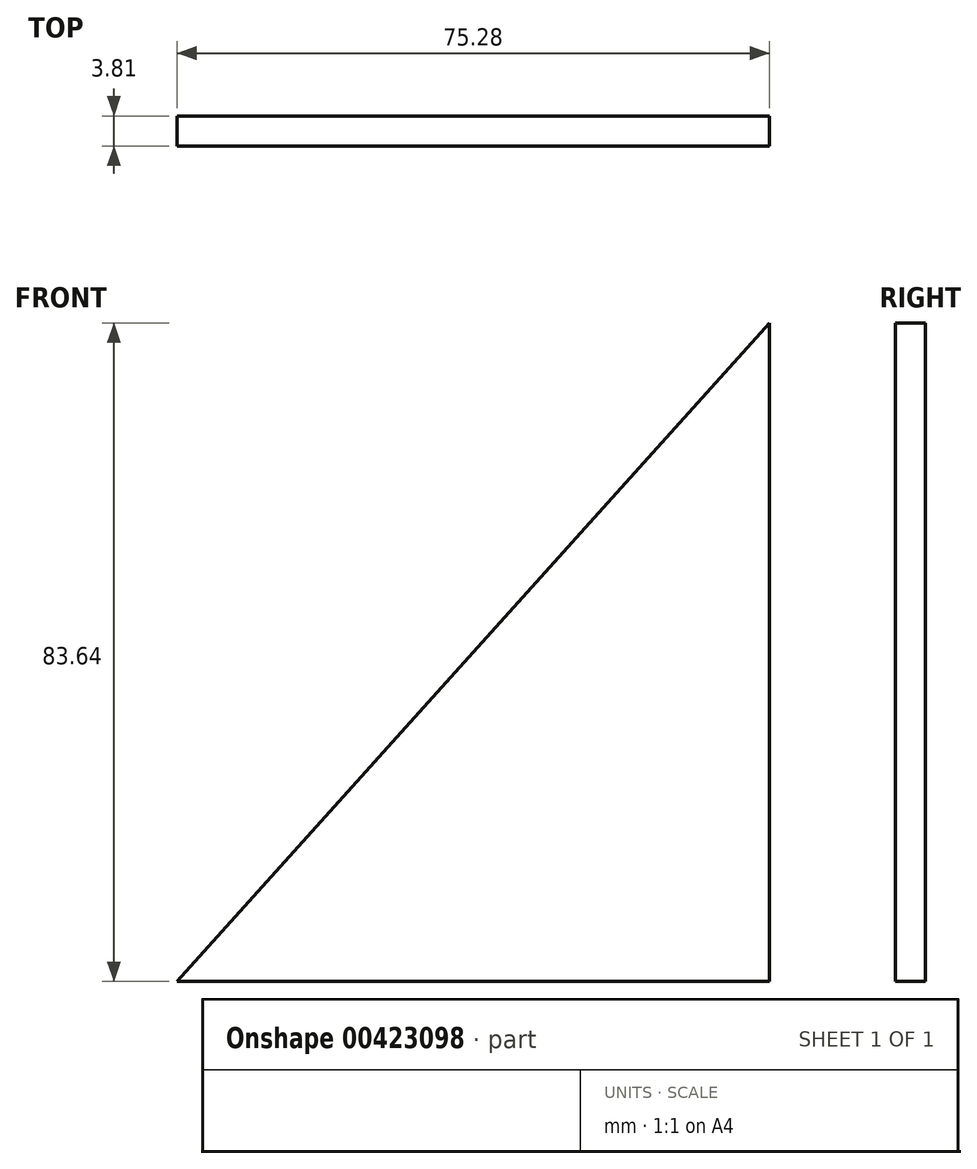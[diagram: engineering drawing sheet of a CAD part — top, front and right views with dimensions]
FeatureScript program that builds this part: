
annotation { "Feature Type Name" : "Feature", "Feature Type Description" : "" }
export const myFeature = defineFeature(function(context is Context, id is Id, definition is map)
    precondition{}
    {
        {
            var Q0;
            Q0=qCreatedBy(makeId("Front.planeOp"),FACE);
            var sketch = newSketch(context, id + "F0", { "sketchPlane" : qUnion([Q0])});
            skLineSegment(sketch, "E0", {"start": v(0, 0) * mm, "end": v(0, 83.64) * mm});
            skLineSegment(sketch, "E1", {"start": v(0, 83.64) * mm, "end": v(-75.28, 0) * mm});
            skLineSegment(sketch, "E2", {"start": v(-75.28, 0) * mm, "end": v(0, 0) * mm});
            skSolve(sketch);
        }
        {
            var Q0;
            Q0=makeQuery(id+"F0.imprint","IMPRINT",FACE,{"disambiguationData":[TD([[makeQuery(id+"F0.imprint","IMPRINT",EDGE,{"derivedFrom":sQuery(id+"F0.wireOp",EDGE,"E0")}),1.0]])]});
            extrude(context, id + "F1", {"entities" : qUnion([Q0]), "depth" : 3.8 * mm});
        }
    });
